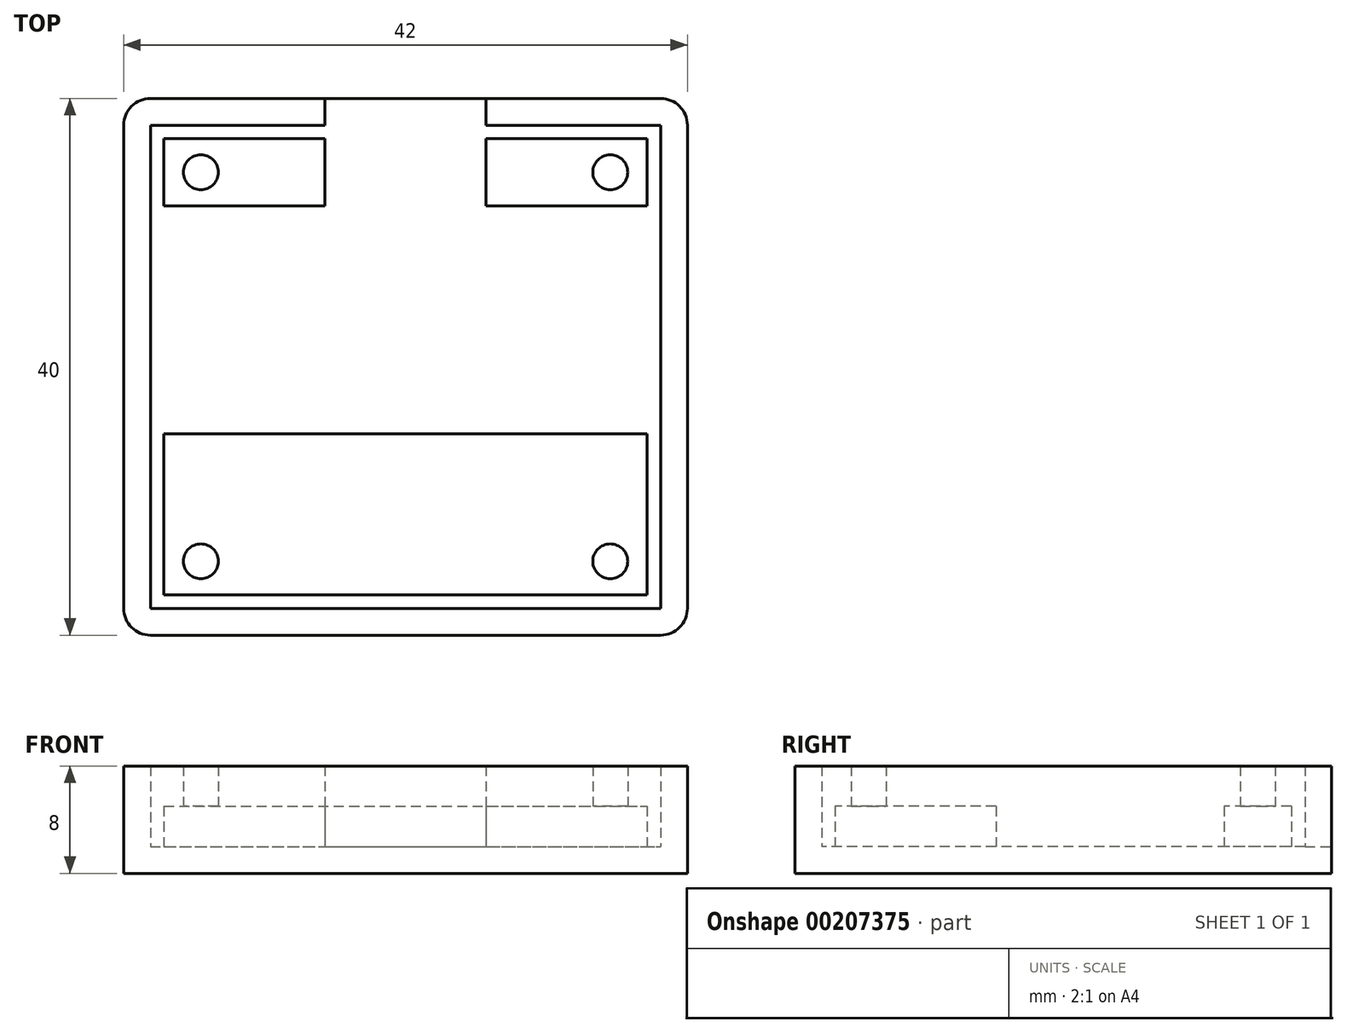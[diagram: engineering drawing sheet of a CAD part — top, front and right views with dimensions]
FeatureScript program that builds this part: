
annotation { "Feature Type Name" : "Feature", "Feature Type Description" : "" }
export const myFeature = defineFeature(function(context is Context, id is Id, definition is map)
    precondition{}
    {
        {
            var Q0;
            Q0=qCreatedBy(makeId("Top.planeOp"),FACE);
            var sketch = newSketch(context, id + "F0", { "sketchPlane" : qUnion([Q0])});
            skLineSegment(sketch, "E0.bottom", {"start": v(-18, 17) * mm, "end": v(18, 17) * mm});
            skLineSegment(sketch, "E0.top", {"start": v(-18, -17) * mm, "end": v(18, -17) * mm});
            skLineSegment(sketch, "E0.left", {"start": v(-18, 17) * mm, "end": v(-18, -17) * mm});
            skLineSegment(sketch, "E0.right", {"start": v(18, 17) * mm, "end": v(18, -17) * mm});
            skPoint(sketch, "E1", {"position": v(-15.25, 14.5) * mm});
            skPoint(sketch, "E2", {"position": v(15.25, 14.5) * mm});
            skPoint(sketch, "E3", {"position": v(15.25, -14.5) * mm});
            skPoint(sketch, "E4", {"position": v(-15.25, -14.5) * mm});
            skPoint(sketch, "E5", {"position": v(0, 17) * mm});
            skPoint(sketch, "E6", {"position": v(18, 0) * mm});
            skLineSegment(sketch, "E7", {"start": v(-15.25, 14.5) * mm, "end": v(15.25, -14.5) * mm, "construction": true});
            skLineSegment(sketch, "E8", {"start": v(-15.25, -14.5) * mm, "end": v(15.25, 14.5) * mm, "construction": true});
            skPoint(sketch, "E9", {"position": v(0, 0) * mm});
            skCircle(sketch, "E10", {"center": v(-15.25, 14.5) * mm, "radius": 1.3 * mm});
            skCircle(sketch, "E11", {"center": v(15.25, 14.5) * mm, "radius": 1.3 * mm});
            skCircle(sketch, "E12", {"center": v(15.25, -14.5) * mm, "radius": 1.3 * mm});
            skCircle(sketch, "E13", {"center": v(-15.25, -14.5) * mm, "radius": 1.3 * mm});
            skLineSegment(sketch, "E14", {"start": v(-18, 12) * mm, "end": v(18, 12) * mm});
            skLineSegment(sketch, "E15", {"start": v(-18, -5) * mm, "end": v(18, -5) * mm});
            skLineSegment(sketch, "E16", {"start": v(-6, 17) * mm, "end": v(-6, 12) * mm});
            skLineSegment(sketch, "E17", {"start": v(6, 17) * mm, "end": v(6, 12) * mm});
            skPoint(sketch, "E17.endSnap0", {"position": v(0, 12) * mm});
            skLineSegment(sketch, "E18.0", {"start": v(-19, 18) * mm, "end": v(-19, -18) * mm});
            skLineSegment(sketch, "E18.1", {"start": v(-19, 18) * mm, "end": v(19, 18) * mm});
            skLineSegment(sketch, "E18.2", {"start": v(19, 18) * mm, "end": v(19, -18) * mm});
            skLineSegment(sketch, "E18.3", {"start": v(-19, -18) * mm, "end": v(19, -18) * mm});
            skLineSegment(sketch, "E19.0", {"start": v(21, 20) * mm, "end": v(21, -20) * mm});
            skLineSegment(sketch, "E19.1", {"start": v(-21, 20) * mm, "end": v(21, 20) * mm});
            skLineSegment(sketch, "E19.2", {"start": v(-21, 20) * mm, "end": v(-21, -20) * mm});
            skLineSegment(sketch, "E19.3", {"start": v(-21, -20) * mm, "end": v(21, -20) * mm});
            skLineSegment(sketch, "E20", {"start": v(-6, 17) * mm, "end": v(-6, 20) * mm});
            skLineSegment(sketch, "E21", {"start": v(6, 17) * mm, "end": v(6, 20) * mm});
            skSolve(sketch);
        }
        {
            var Q0;
            {var subQ1=sQuery(id+"F0.wireOp",EDGE,"E0.top");Q0=makeQuery(id+"F0.imprint","IMPRINT",FACE,{"disambiguationData":[TD([[makeQuery(id+"F0.imprint","IMPRINT",EDGE,{"derivedFrom":subQ1}),1.0]])]});}
            var Q1;
            Q1=makeQuery(id+"F0.imprint","IMPRINT",FACE,{"disambiguationData":[TD([[makeQuery(id+"F0.imprint","IMPRINT",EDGE,{"derivedFrom":sQuery(id+"F0.wireOp",EDGE,"E10")}),-1.0]])]});
            var Q2;
            Q2=makeQuery(id+"F0.imprint","IMPRINT",FACE,{"disambiguationData":[TD([[makeQuery(id+"F0.imprint","IMPRINT",EDGE,{"derivedFrom":sQuery(id+"F0.wireOp",EDGE,"E11")}),-1.0]])]});
            extrude(context, id + "F1", {"entities" : qUnion([Q0, Q1, Q2]), "depth" : 5 * mm, "offsetDistance" : 25 * mm});
        }
        {
            var Q0;
            {var subQ0=sQuery(id+"F0.wireOp",EDGE,"E14");Q0=makeQuery(id+"F0.imprint","IMPRINT",FACE,{"disambiguationData":[TD([[makeQuery(id+"F0.imprint","IMPRINT",EDGE,{"derivedFrom":subQ0}),-1.0]])]});}
            var Q1;
            {var subQ0=sQuery(id+"F0.wireOp",EDGE,"E16");Q1=makeQuery(id+"F0.imprint","IMPRINT",FACE,{"disambiguationData":[TD([[makeQuery(id+"F0.imprint","IMPRINT",EDGE,{"derivedFrom":subQ0}),1.0]])]});}
            var Q2;
            {var subQ1=sQuery(id+"F0.wireOp",EDGE,"E0.top");Q2=makeQuery(id+"F0.imprint","IMPRINT",FACE,{"disambiguationData":[TD([[makeQuery(id+"F0.imprint","IMPRINT",EDGE,{"derivedFrom":subQ1}),-1.0]])]});}
            var Q3;
            {var subQ0=sQuery(id+"F0.wireOp",EDGE,"E20");var subQ5=sQuery(id+"F0.wireOp",EDGE,"E18.1");var subQ6=makeQuery(id+"F0.imprint","INTERSECT",VERTEX,{"derivedFrom":[subQ5,subQ0]});Q3=makeQuery(id+"F0.imprint","IMPRINT",FACE,{"disambiguationData":[TD([[makeQuery(id+"F0.imprint","IMPRINT",EDGE,{"disambiguationData":[TD([[subQ6,-1.0]])],"derivedFrom":subQ5}),-1.0]])]});}
            var Q4;
            {var subQ0=sQuery(id+"F0.wireOp",EDGE,"E20");var subQ1=sQuery(id+"F0.wireOp",EDGE,"E18.1");var subQ2=makeQuery(id+"F0.imprint","INTERSECT",VERTEX,{"derivedFrom":[subQ1,subQ0]});Q4=makeQuery(id+"F0.imprint","IMPRINT",FACE,{"disambiguationData":[TD([[makeQuery(id+"F0.imprint","IMPRINT",EDGE,{"disambiguationData":[TD([[subQ2,-1.0]])],"derivedFrom":subQ1}),1.0]])]});}
            extrude(context, id + "F2", {"entities" : qUnion([Q0, Q1, Q2, Q3, Q4]), "operationType" : NewBodyOperationType.ADD, "depth" : 2 * mm, "offsetDistance" : 25 * mm});
        }
        {
            var Q0;
            Q0=makeQuery(id+"F0.imprint","IMPRINT",FACE,{"disambiguationData":[TD([[makeQuery(id+"F0.imprint","IMPRINT",EDGE,{"derivedFrom":sQuery(id+"F0.wireOp",EDGE,"E10")}),1.0]])]});
            var Q1;
            Q1=makeQuery(id+"F0.imprint","IMPRINT",FACE,{"disambiguationData":[TD([[makeQuery(id+"F0.imprint","IMPRINT",EDGE,{"derivedFrom":sQuery(id+"F0.wireOp",EDGE,"E11")}),1.0]])]});
            var Q2;
            Q2=makeQuery(id+"F0.imprint","IMPRINT",FACE,{"disambiguationData":[TD([[makeQuery(id+"F0.imprint","IMPRINT",EDGE,{"derivedFrom":sQuery(id+"F0.wireOp",EDGE,"E12")}),1.0]])]});
            var Q3;
            Q3=makeQuery(id+"F0.imprint","IMPRINT",FACE,{"disambiguationData":[TD([[makeQuery(id+"F0.imprint","IMPRINT",EDGE,{"derivedFrom":sQuery(id+"F0.wireOp",EDGE,"E13")}),1.0]])]});
            var Q4;
            Q4=makeQuery(id+"F0.imprint","IMPRINT",FACE,{"disambiguationData":[TD([[makeQuery(id+"F0.imprint","IMPRINT",EDGE,{"derivedFrom":sQuery(id+"F0.wireOp",EDGE,"E18.0")}),-1.0]])]});
            extrude(context, id + "F3", {"entities" : qUnion([Q0, Q1, Q2, Q3, Q4]), "operationType" : NewBodyOperationType.ADD, "depth" : 8 * mm, "offsetDistance" : 25 * mm});
        }
        {
            var Q0;
            Q0=makeQuery(id+"F3.opExtrude","SWEPT_EDGE",EDGE,{"disambiguationData":[OSD([sQuery(id+"F0.wireOp",EDGE,"E19.2"),sQuery(id+"F0.wireOp",EDGE,"E19.3")])]});
            var Q1;
            Q1=makeQuery(id+"F3.opExtrude","SWEPT_EDGE",EDGE,{"disambiguationData":[OSD([sQuery(id+"F0.wireOp",EDGE,"E19.0"),sQuery(id+"F0.wireOp",EDGE,"E19.3")])]});
            var Q2;
            Q2=makeQuery(id+"F3.opExtrude","SWEPT_EDGE",EDGE,{"disambiguationData":[OSD([sQuery(id+"F0.wireOp",EDGE,"E19.0"),sQuery(id+"F0.wireOp",EDGE,"E19.1")])]});
            var Q3;
            Q3=makeQuery(id+"F3.opExtrude","SWEPT_EDGE",EDGE,{"disambiguationData":[OSD([sQuery(id+"F0.wireOp",EDGE,"E19.1"),sQuery(id+"F0.wireOp",EDGE,"E19.2")])]});
            fillet(context, id + "F4", {"entities" : qUnion([Q0, Q1, Q2, Q3]), "radius" : 2 * mm, "tangentPropagation" : true, "allowEdgeOverflow" : false});
        }
    });
